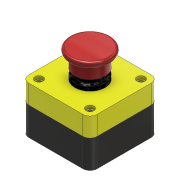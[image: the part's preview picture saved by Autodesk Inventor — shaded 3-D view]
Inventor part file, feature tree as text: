
AUTODESK INVENTOR PART (.ipt)
format: ipt  version: 2022 (Build 260153000, 153)  size: 297,984 bytes
history: native  units: mm
features: extrude x11, sketch x11, fillet x3, projected_geometry x2
ambient origin geometry x8: Origin, YZ Plane, XZ Plane, XY Plane, X Axis, Y Axis, Z Axis, Center Point
bodies: Solid1 (feature_tree), Solid2 (feature_tree)
feature tree (27):
  extrude  "Extrusion1"  Depth=34.0mm
  extrude  "Extrusion2"  Depth=34.0mm
  extrude  "Extrusion3"  Depth=30.0mm
  extrude  "Extrusion4"  Depth=4.0mm
  extrude  "Extrusion5"  Depth=30.0mm
  fillet  "Fillet1"  Radius=12.0mm
  fillet  "Fillet2"  Radius=40.0mm
  fillet  "Fillet3"  Radius=6.0mm
  extrude  "Extrusion6"  Depth=3.0mm
  extrude  "Extrusion7"  Depth=5.0mm
  extrude  "Extrusion8"  Depth=5.0mm
  extrude  "Extrusion9"  Depth=5.0mm
  extrude  "Extrusion10"  Depth=20.0mm
  extrude  "Extrusion11"  Depth=3.0mm
  sketch  "Sketch1"  dims[d0=34.0mm d1=34.0mm]
  sketch  "Sketch2"  dims[d2=34.0mm d3=34.0mm]
  sketch  "Sketch3"  dims[d4=19.0mm d5=0.0mm d6=30.0mm]
  sketch  "Sketch4"  dims[d7=4.0mm d8=0.0mm d9=22.5mm]
  sketch  "Sketch5"  dims[d10=6.0mm d11=0.0mm d12=30.0mm d13=12.0mm d14=0.0mm d15=40.0mm d16=6.0mm d17=0.0mm]
  sketch  "Sketch6"  dims[d18=2.0mm d19=3.0mm]
  sketch  "Sketch7"  dims[d20=7.0mm d21=5.0mm]
  sketch  "Sketch8"  dims[d22=25.4mm d23=5.0mm]
  sketch  "Sketch9"  dims[d24=5.0mm d25=5.0mm]
  projected_geometry  "Projected Loop1"
  sketch  "Sketch10"  dims[d26=20.0mm d27=0.0mm d28=8.0mm]
  sketch  "Sketch11"  dims[d29=8.0mm d30=8.0mm d31=8.0mm d32=3.0mm d33=0.0mm d34=18.0mm d35=18.0mm d36=29.0mm d37=29.0mm d38=5.0mm d39=25.0mm d40=0.0mm d41=10.0mm d42=0.0mm d43=10.0mm d44=10.0mm d45=0.0mm d46=3.0mm d47=0.0mm]
  projected_geometry  "Projected Loop2"
